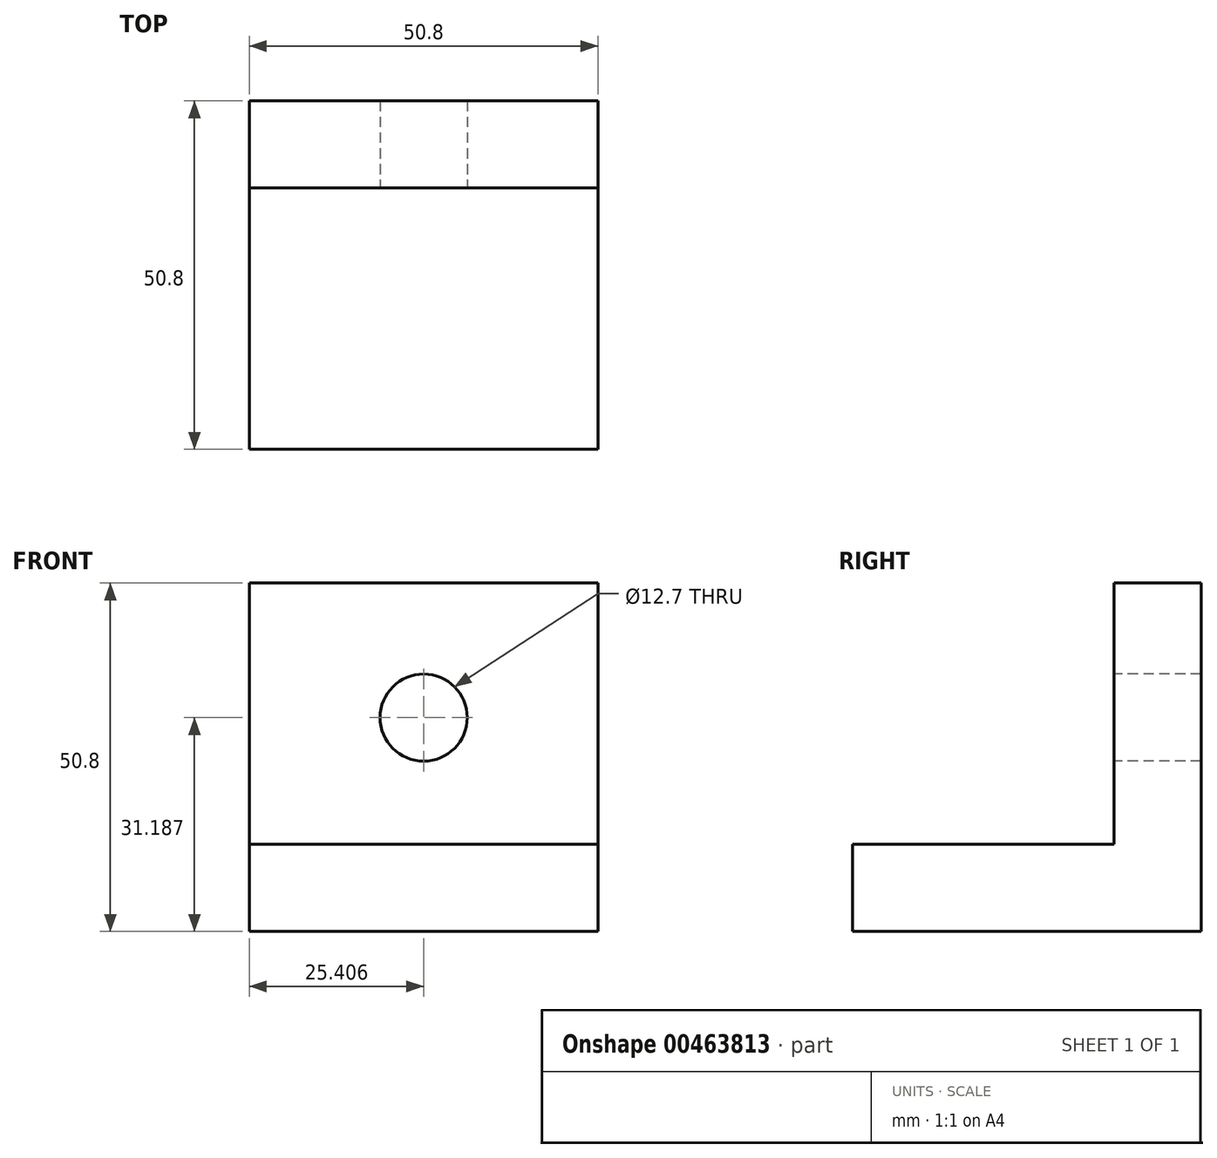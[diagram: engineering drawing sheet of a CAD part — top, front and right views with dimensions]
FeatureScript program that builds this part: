
annotation { "Feature Type Name" : "Feature", "Feature Type Description" : "" }
export const myFeature = defineFeature(function(context is Context, id is Id, definition is map)
    precondition{}
    {
        {
            var Q0;
            Q0=qCreatedBy(makeId("Top.planeOp"),FACE);
            var sketch = newSketch(context, id + "F0", { "sketchPlane" : qUnion([Q0])});
            skLineSegment(sketch, "E0", {"start": v(0, 0) * mm, "end": v(0, 50.8) * mm});
            skLineSegment(sketch, "E1", {"start": v(0, 50.8) * mm, "end": v(50.8, 50.8) * mm});
            skLineSegment(sketch, "E2", {"start": v(50.8, 50.8) * mm, "end": v(50.8, 0) * mm});
            skLineSegment(sketch, "E3", {"start": v(50.8, 0) * mm, "end": v(0, 0) * mm});
            skSolve(sketch);
        }
        {
            var Q0;
            Q0=makeQuery(id+"F0.imprint","IMPRINT",FACE,{"disambiguationData":[TD([[makeQuery(id+"F0.imprint","IMPRINT",EDGE,{"derivedFrom":sQuery(id+"F0.wireOp",EDGE,"E0")}),-1.0]])]});
            extrude(context, id + "F1", {"entities" : qUnion([Q0]), "depth" : 12.7 * mm});
        }
        {
            var Q0;
            Q0=makeQuery(id+"F1.opExtrude","CAP_FACE",FACE,{"disambiguationData":[OSD([sQuery(id+"F0.wireOp",EDGE,"E0"),sQuery(id+"F0.wireOp",EDGE,"E1"),sQuery(id+"F0.wireOp",EDGE,"E2"),sQuery(id+"F0.wireOp",EDGE,"E3")])],"isStart":false});
            var sketch = newSketch(context, id + "F2", { "sketchPlane" : qUnion([Q0])});
            skLineSegment(sketch, "E4", {"start": v(0, 38.1) * mm, "end": v(50.8, 38.1) * mm});
            skSolve(sketch);
        }
        {
            var Q0;
            Q0 = qSketchRegion(id + "F2", true);
            var Q1;
            {var subQ0=sQuery(id+"F2.wireOp",EDGE,"E4");Q1=makeQuery(id+"F2.imprint","IMPRINT",FACE,{"disambiguationData":[TD([[makeQuery(id+"F2.imprint","IMPRINT",EDGE,{"derivedFrom":subQ0}),1.0]])]});}
            extrude(context, id + "F3", {"entities" : qUnion([Q0, Q1]), "operationType" : NewBodyOperationType.ADD, "depth" : 38.1 * mm});
        }
        {
            var Q0;
            Q0=makeQuery(id+"F3.opExtrude","SWEPT_FACE",FACE,{"disambiguationData":[OSD([sQuery(id+"F2.wireOp",EDGE,"E4")])]});
            var sketch = newSketch(context, id + "F4", { "sketchPlane" : qUnion([Q0])});
            skCircle(sketch, "E5", {"center": v(25.4, 31.19) * mm, "radius": 6.35 * mm});
            skSolve(sketch);
        }
        {
            var Q0;
            Q0=sQuery(id+"F4.wireOp",VERTEX,"E5.center");
            var Q1;
            Q1=makeQuery(id+"F1.opExtrude","SWEPT_BODY",BODY,{"disambiguationData":[OSD([sQuery(id+"F0.wireOp",EDGE,"E0"),sQuery(id+"F0.wireOp",EDGE,"E1"),sQuery(id+"F0.wireOp",EDGE,"E2"),sQuery(id+"F0.wireOp",EDGE,"E3")])]});
            hole(context, id + "F5", {"style" : HoleStyle.SIMPLE, "endStyle" : HoleEndStyle.BLIND, "holeDiameter" : 12.7 * mm, "holeDepth" : 50.8 * mm, "isTappedThrough" : true, "tappedDepth" : 12.7 * mm, "tapClearance" : 3, "locations" : qUnion([Q0]), "scope" : qUnion([Q1])});
        }
    });
